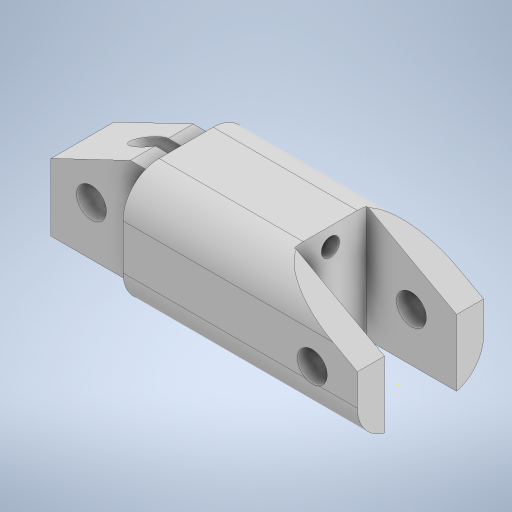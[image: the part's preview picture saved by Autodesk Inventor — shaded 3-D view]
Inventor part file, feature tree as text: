
AUTODESK INVENTOR PART (.ipt)
format: ipt  version: 2024 (Build 280153000, 153)  size: 633,344 bytes
history: native  units: mm
features: sketch x32, extrude x28, move_body x6, plane x4, split x4, boolean_combine x4, chamfer x3, fillet x1
ambient origin geometry x8: Origin, YZ Plane, XZ Plane, XY Plane, X Axis, Y Axis, Z Axis, Center Point
bodies: Solid1 (feature_tree), Solid2 (feature_tree), Solid3 (feature_tree), Solid6 (feature_tree), Solid7 (feature_tree), Solid8 (feature_tree), Solid9 (feature_tree), Solid10 (feature_tree), Solid11 (feature_tree)
feature tree (82):
  extrude  "Extrusion1"  Depth=16.0mm
  sketch  "Sketch2"  dims[d2=15.0mm d3=0.0mm d4=10.0mm]
  extrude  "Extrusion2"  Depth=10.0mm
  chamfer  "Chamfer1"  Distance=21.25mm
  extrude  "Extrusion3"  Depth=10.0mm TaperAngle=0.0deg
  extrude  "Extrusion4"  Depth=11.5mm TaperAngle=0.0deg
  extrude  "Extrusion5"  Depth=1.0mm TaperAngle=0.0deg
  chamfer  "Chamfer2"  Distance=6.0mm Angle=45.0deg
  sketch  "Sketch6"  dims[d14=7.0mm d15=11.5mm d16=0.0mm]
  extrude  "Extrusion6"  Depth=9.0mm
  extrude  "Extrusion7"  Depth=45.25mm TaperAngle=0.0deg
  chamfer  "Chamfer3"  Distance=11.5mm Angle=45.0deg
  sketch  "Sketch9"  dims[d26=3.3mm d27=45.25mm d28=0.0mm d29=11.5mm d30=5.5mm d31=45.0deg]
  extrude  "Extrusion8"  Depth=65.75mm TaperAngle=0.0deg
  extrude  "Extrusion9"  Depth=9.0mm TaperAngle=0.0deg
  extrude  "Extrusion10"  Depth=13.0mm TaperAngle=0.0deg
  sketch  "Sketch13"  dims[d43=24.0mm d44=21.0mm d45=0.0mm]
  extrude  "Extrusion11"  Depth=21.0mm TaperAngle=0.0deg
  extrude  "Extrusion12"  TaperAngle=0.0deg  [1 undecoded]
  extrude  "Extrusion13"  Depth=6.0mm TaperAngle=0.0deg
  plane  "Work Plane1"
  split  "Split1"
  move_body  "Move Body1"
  extrude  "Extrusion14"  Depth=0.5mm TaperAngle=0.0deg
  move_body  "Move Body2"
  extrude  "Extrusion15"  Depth=10.0mm
  sketch  "Sketch19"  dims[d70=31.0mm d71=29.5mm d72=0.0mm]
  sketch  "Sketch20"  dims[d74=11.0mm d75=1.0mm]
  extrude  "Extrusion16"  Depth=10.0mm
  extrude  "Extrusion18"  Depth=29.5mm TaperAngle=0.0deg
  extrude  "Extrusion19"  Depth=1.0mm
  extrude  "Extrusion20"  Depth=10.0mm TaperAngle=0.0deg
  boolean_combine  "Combine1"
  plane  "Work Plane3"
  split  "Split3"
  extrude  "Extrusion21"  TaperAngle=0.0deg  [1 undecoded]
  plane  "Work Plane4"
  split  "Split4"
  move_body  "Move Body3"
  move_body  "Move Body4"
  boolean_combine  "Combine3"
  extrude  "Extrusion22"  Depth=1.0mm TaperAngle=0.0deg
  extrude  "Extrusion23"  Depth=12.5mm TaperAngle=0.0deg
  extrude  "Extrusion24"  TaperAngle=0.0deg  [1 undecoded]
  extrude  "Extrusion25"  Depth=46.5mm TaperAngle=0.0deg
  move_body  "Move Body5"
  sketch  "Sketch32"  dims[d102=46.5mm d103=0.0mm d104=4.0mm d105=1.0mm]
  boolean_combine  "Combine4"
  extrude  "Extrusion26"  Depth=2.0mm
  extrude  "Extrusion27"  Depth=4.0mm
  fillet  "Fillet2"  Radius=1.0mm
  sketch  "Sketch34"  dims[d109=5.5mm d110=4.0mm d111=0.0mm d112=0.0mm]
  extrude  "Extrusion28"  Depth=46.5mm TaperAngle=0.0deg
  plane  "Work Plane5"
  split  "Split5"
  move_body  "Move Body6"
  extrude  "Extrusion29"  Depth=4.0mm TaperAngle=0.0deg
  boolean_combine  "Combine5"
  sketch  "Sketch1"  dims[d0=36.0mm d1=16.0mm]
  sketch  "Sketch3"  dims[d5=10.0mm]
  sketch  "Sketch4"  dims[d6=3.3mm d7=21.25mm d8=0.0mm]
  sketch  "Sketch5"  dims[d9=10.0mm d10=5.5mm d11=45.0deg d12=10.0mm d13=0.0mm]
  sketch  "Sketch7"  dims[d17=3.3mm d18=1.0mm d19=0.0mm d20=6.0mm d21=11.5mm d22=45.0deg]
  sketch  "Sketch8"  dims[d23=15.0mm d24=0.0mm d25=9.0mm]
  sketch  "Sketch10"  dims[d32=2.0mm d33=65.75mm d34=0.0mm]
  sketch  "Sketch11"  dims[d35=0.5mm d36=0.0mm d37=9.0mm d38=0.0mm]
  sketch  "Sketch12"  dims[d39=0.5mm d40=0.0mm d41=13.0mm d42=0.0mm]
  sketch  "Sketch14"  dims[d46=12.25mm d47=-12.0mm d48=0.0mm d49=0.0mm]
  sketch  "Sketch15"  dims[d50=30.0mm d51=0.0mm d52=6.0mm d53=0.0mm d54=0.0mm]
  sketch  "Sketch16"  dims[d56=0.5mm d57=0.0mm d58=0.5mm d59=0.0mm]
  sketch  "Sketch17"  dims[d64=10.0mm d65=0.0mm d66=3.0mm]
  sketch  "Sketch18"  dims[d67=10.0mm d68=0.0mm d69=1.0mm]
  sketch  "Sketch22"  dims[d76=1.0mm d77=10.0mm d78=0.0mm]
  sketch  "Sketch25"  dims[d79=5.5mm d80=0.0mm d81=0.0mm d82=-1.0mm]
  sketch  "Sketch27"  dims[d83=0.0mm d84=0.0mm d85=1.0mm d86=1.0mm d87=0.0mm]
  sketch  "Sketch28"  dims[d88=1.0mm d89=0.0mm d90=12.5mm d91=0.0mm]
  sketch  "Sketch29"  dims[d92=19.0mm d93=0.0mm d94=-12.0mm d95=0.0mm d96=0.0mm]
  sketch  "Sketch30"  dims[d97=2.0mm d98=46.5mm d99=0.0mm]
  sketch  "Sketch31"  dims[d100=2.0mm d101=2.0mm]
  sketch  "Sketch33"  dims[d106=19.0mm d107=46.5mm d108=0.0mm]
  sketch  "Sketch35"  dims[d113=15.0mm d114=0.0mm]
  sketch  "Sketch36"  dims[d115=0.5mm d116=0.872665mm]
note: 3 required parameter values undecoded (feature->parameter linkage not recoverable at this tier; creation-order binding heuristic only, values carry confidence <= 0.55)
